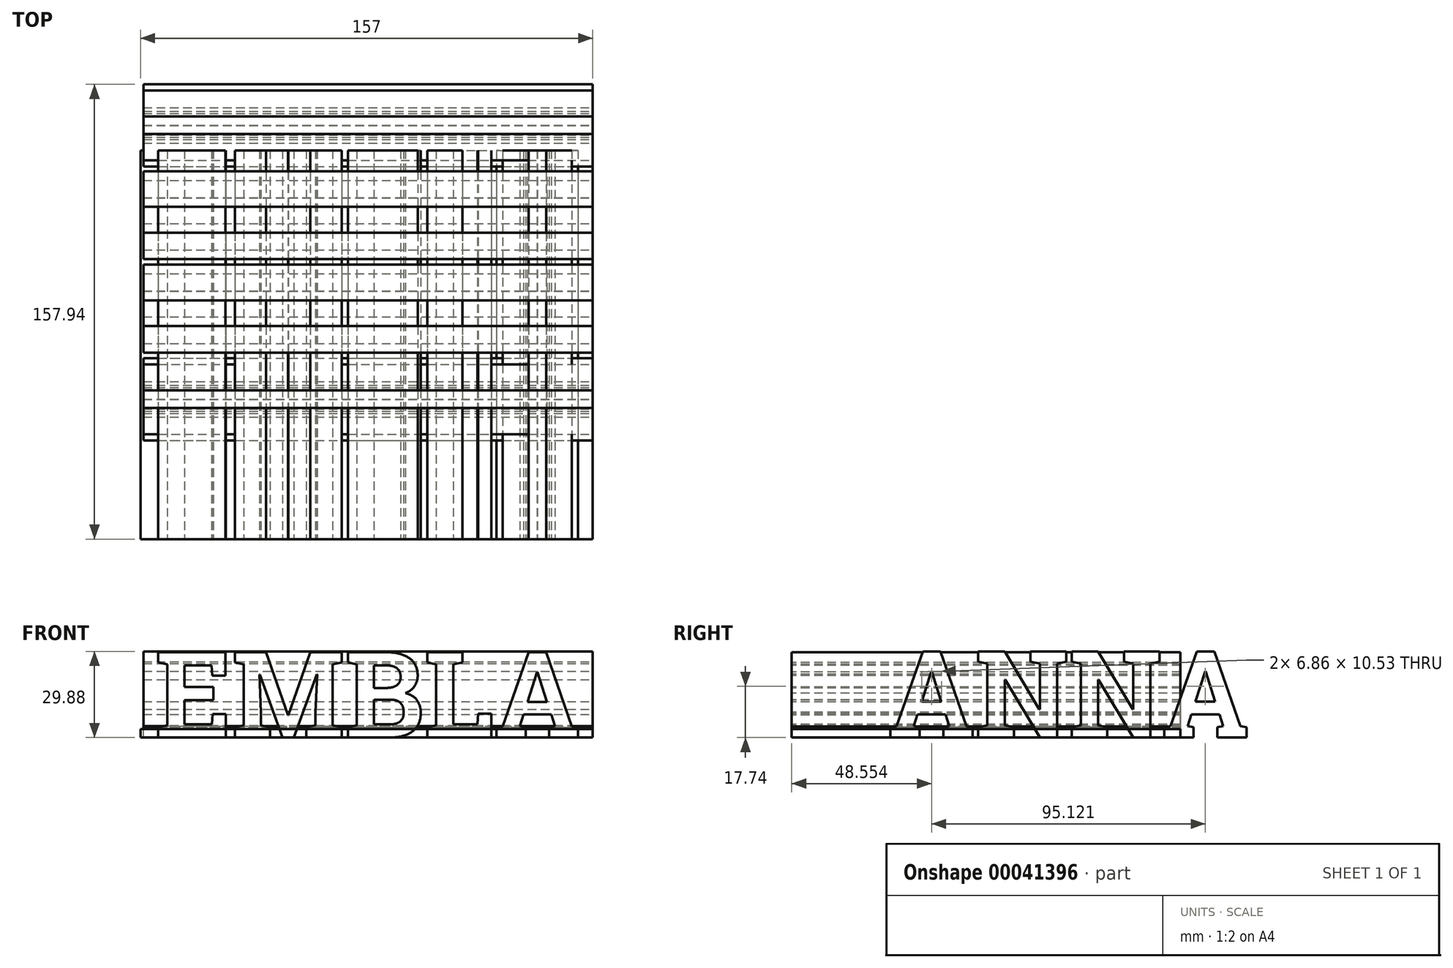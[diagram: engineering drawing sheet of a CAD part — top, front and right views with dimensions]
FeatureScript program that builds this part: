
annotation { "Feature Type Name" : "Feature", "Feature Type Description" : "" }
export const myFeature = defineFeature(function(context is Context, id is Id, definition is map)
    precondition{}
    {
        {
            var Q0;
            Q0=qCreatedBy(makeId("Top.planeOp"),FACE);
            var sketch = newSketch(context, id + "F0", { "sketchPlane" : qUnion([Q0])});
            skLineSegment(sketch, "E0.rect.bottom", {"start": v(78.5, 67.5) * mm, "end": v(-78.5, 67.5) * mm});
            skLineSegment(sketch, "E0.rect.top", {"start": v(78.5, -67.5) * mm, "end": v(-78.5, -67.5) * mm});
            skLineSegment(sketch, "E0.rect.left", {"start": v(78.5, 67.5) * mm, "end": v(78.5, -67.5) * mm});
            skLineSegment(sketch, "E0.rect.right", {"start": v(-78.5, 67.5) * mm, "end": v(-78.5, -67.5) * mm});
            skPoint(sketch, "E0.rect.middle", {"position": v(0, 0) * mm});
            skSolve(sketch);
        }
        {
            var Q0;
            Q0=makeQuery(id+"F0.imprint","IMPRINT",FACE,{"disambiguationData":[TD([[makeQuery(id+"F0.imprint","IMPRINT",EDGE,{"derivedFrom":sQuery(id+"F0.wireOp",EDGE,"E0.rect.bottom")}),1.0]])]});
            extrude(context, id + "F1", {"entities" : qUnion([Q0]), "depth" : 3 * mm});
        }
        {
            var Q0;
            Q0 = qSketchRegion(id + "F0", true);
            extrude(context, id + "F2", {"entities" : qUnion([Q0]), "depth" : 3 * mm});
        }
        {
            var Q0;
            Q0=makeQuery(id+"F2.opExtrude","SWEPT_FACE",FACE,{"disambiguationData":[OSD([sQuery(id+"F0.wireOp",EDGE,"E0.rect.top")])]});
            var sketch = newSketch(context, id + "F3", { "sketchPlane" : qUnion([Q0])});
            skText(sketch, "E1", { "text": "EMBLA", "fontName": "RobotoSlab-Bold.ttf"});
            const initialGuessF3  = {"E1": [-0.0735, 0, 1, 0, 0.03]};
            skSetInitialGuess(sketch, initialGuessF3);
            skSolve(sketch);
        }
        {
            var Q0;
            Q0=makeQuery(id+"F1.opExtrude","SWEPT_FACE",FACE,{"disambiguationData":[OSD([sQuery(id+"F0.wireOp",EDGE,"E0.rect.left")])]});
            var sketch = newSketch(context, id + "F4", { "sketchPlane" : qUnion([Q0])});
            skText(sketch, "E2", { "text": "ANNA", "fontName": "RobotoSlab-Bold.ttf"});
            const initialGuessF4  = {"E2": [-0.03405, 0, 1, 0, 0.03026]};
            skSetInitialGuess(sketch, initialGuessF4);
            skSolve(sketch);
        }
        {
            var Q0;
            Q0 = qSketchRegion(id + "F3", true);
            extrude(context, id + "F5", {"entities" : qUnion([Q0]), "oppositeDirection" : true, "depth" : 135 * mm});
        }
        {
            var Q0;
            Q0 = qSketchRegion(id + "F4", true);
            extrude(context, id + "F6", {"entities" : qUnion([Q0]), "oppositeDirection" : true, "depth" : 156 * mm});
        }
        {
            var Q0;
            Q0=makeQuery(id+"F1.opExtrude","SWEPT_BODY",BODY,{"disambiguationData":[OSD([sQuery(id+"F0.wireOp",EDGE,"E0.rect.bottom"),sQuery(id+"F0.wireOp",EDGE,"E0.rect.top"),sQuery(id+"F0.wireOp",EDGE,"E0.rect.left"),sQuery(id+"F0.wireOp",EDGE,"E0.rect.right")])]});
            var Q1;
            Q1=makeQuery(id+"F2.opExtrude","SWEPT_BODY",BODY,{"disambiguationData":[OSD([sQuery(id+"F0.wireOp",EDGE,"E0.rect.bottom"),sQuery(id+"F0.wireOp",EDGE,"E0.rect.top"),sQuery(id+"F0.wireOp",EDGE,"E0.rect.left"),sQuery(id+"F0.wireOp",EDGE,"E0.rect.right")])]});
            booleanBodies(context, id + "F7", {"operationType" : BooleanOperationType.INTERSECTION, "tools" : qUnion([Q0, Q1])});
        }
    });
